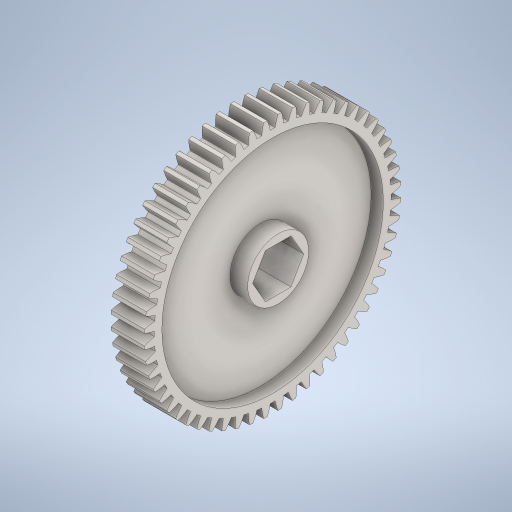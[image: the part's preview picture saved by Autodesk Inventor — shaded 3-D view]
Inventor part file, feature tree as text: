
AUTODESK INVENTOR PART (.ipt)
format: ipt  version: 2023 (Build 270158030, 158C)  size: 540,672 bytes
history: native  units: in
note: dims shown in document units (in); Inventor stores cm internally (conversion verified against a paired STEP export)
features: sketch x1, other x1
ambient origin geometry x8: Origin, YZ Plane, XZ Plane, XY Plane, X Axis, Y Axis, Z Axis, Center Point
bodies: Solid1 (feature_tree)
feature tree (2):
  sketch  "Sketch1"  dims[d0=2.8in]
  other  "Bore"
